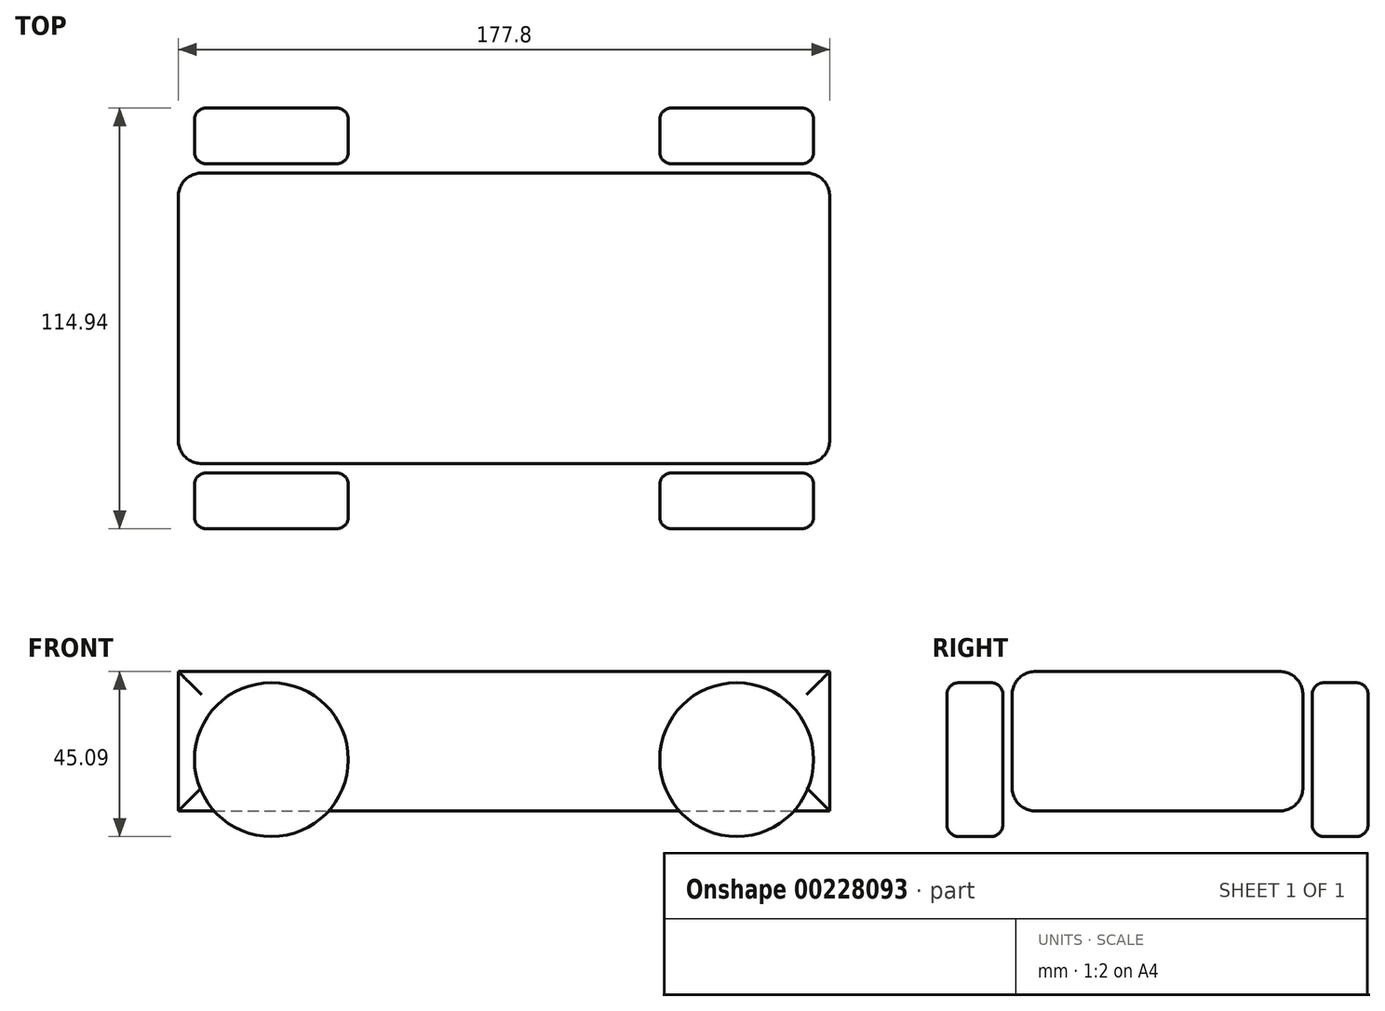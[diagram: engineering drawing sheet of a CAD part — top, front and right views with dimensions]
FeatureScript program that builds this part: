
annotation { "Feature Type Name" : "Feature", "Feature Type Description" : "" }
export const myFeature = defineFeature(function(context is Context, id is Id, definition is map)
    precondition{}
    {
        {
            var Q0;
            Q0=qCreatedBy(makeId("Front.planeOp"),FACE);
            var sketch = newSketch(context, id + "F0", { "sketchPlane" : qUnion([Q0])});
            skLineSegment(sketch, "E0.bottom", {"start": v(-88.9, 19.05) * mm, "end": v(88.9, 19.05) * mm});
            skLineSegment(sketch, "E0.top", {"start": v(-88.9, -19.05) * mm, "end": v(88.9, -19.05) * mm});
            skLineSegment(sketch, "E0.left", {"start": v(-88.9, 19.05) * mm, "end": v(-88.9, -19.05) * mm});
            skLineSegment(sketch, "E0.right", {"start": v(88.9, 19.05) * mm, "end": v(88.9, -19.05) * mm});
            skPoint(sketch, "E0.middle", {"position": v(0, 0) * mm});
            skLineSegment(sketch, "E1", {"start": v(-109.46, -26.03) * mm, "end": v(110.9, -26.04) * mm, "construction": true});
            skCircle(sketch, "E2", {"center": v(63.5, -5.03) * mm, "radius": 21 * mm});
            skSolve(sketch);
        }
        {
            var Q0;
            Q0=qCreatedBy(makeId("Front.planeOp"),FACE);
            var sketch = newSketch(context, id + "F1", { "sketchPlane" : qUnion([Q0])});
            skLineSegment(sketch, "E3.0", {"start": v(-88.9, 19.05) * mm, "end": v(88.9, 19.05) * mm});
            skLineSegment(sketch, "E3.1", {"start": v(-88.9, 19.05) * mm, "end": v(-88.9, -19.05) * mm});
            skLineSegment(sketch, "E3.2", {"start": v(-88.9, -19.05) * mm, "end": v(88.9, -19.05) * mm});
            skLineSegment(sketch, "E3.3", {"start": v(88.9, 19.05) * mm, "end": v(88.9, -19.05) * mm});
            skSolve(sketch);
        }
        {
            var Q0;
            Q0 = qSketchRegion(id + "F1", true);
            extrude(context, id + "F2", {"entities" : qUnion([Q0]), "endBound" : BoundingType.SYMMETRIC, "depth" : 79.38 * mm});
        }
        {
            var Q0;
            Q0=makeQuery(id+"F2.opExtrude","CAP_FACE",FACE,{"disambiguationData":[OSD([sQuery(id+"F1.wireOp",EDGE,"E3.0"),sQuery(id+"F1.wireOp",EDGE,"E3.1"),sQuery(id+"F1.wireOp",EDGE,"E3.2"),sQuery(id+"F1.wireOp",EDGE,"E3.3")])],"isStart":false});
            cPlane(context, id + "F3", {"entities" : qUnion([Q0]), "cplaneType" : CPlaneType.OFFSET, "offset" : 2.54 * mm, "width" : 152.4 * mm, "height" : 152.4 * mm});
        }
        {
            var Q0;
            Q0=qCreatedBy(id+"F3.planeOp",FACE);
            var sketch = newSketch(context, id + "F4", { "sketchPlane" : qUnion([Q0])});
            skCircle(sketch, "E4.0", {"center": v(63.5, -5.03) * mm, "radius": 21 * mm});
            skSolve(sketch);
        }
        {
            var Q0;
            Q0 = qSketchRegion(id + "F4", true);
            extrude(context, id + "F5", {"entities" : qUnion([Q0]), "depth" : 15.24 * mm});
        }
        {
            var Q0;
            Q0=makeQuery(id+"F2.opExtrude","CAP_EDGE",EDGE,{"disambiguationData":[OSD([sQuery(id+"F1.wireOp",EDGE,"E3.0")])],"isStart":false});
            var Q1;
            Q1=makeQuery(id+"F2.opExtrude","CAP_EDGE",EDGE,{"disambiguationData":[OSD([sQuery(id+"F1.wireOp",EDGE,"E3.2")])],"isStart":false});
            var Q2;
            Q2=makeQuery(id+"F2.opExtrude","CAP_EDGE",EDGE,{"disambiguationData":[OSD([sQuery(id+"F1.wireOp",EDGE,"E3.1")])],"isStart":false});
            var Q3;
            Q3=makeQuery(id+"F2.opExtrude","CAP_EDGE",EDGE,{"disambiguationData":[OSD([sQuery(id+"F1.wireOp",EDGE,"E3.3")])],"isStart":false});
            var Q4;
            Q4=makeQuery(id+"F2.opExtrude","CAP_EDGE",EDGE,{"disambiguationData":[OSD([sQuery(id+"F1.wireOp",EDGE,"E3.0")])],"isStart":true});
            var Q5;
            Q5=makeQuery(id+"F2.opExtrude","CAP_EDGE",EDGE,{"disambiguationData":[OSD([sQuery(id+"F1.wireOp",EDGE,"E3.3")])],"isStart":true});
            var Q6;
            Q6=makeQuery(id+"F2.opExtrude","CAP_EDGE",EDGE,{"disambiguationData":[OSD([sQuery(id+"F1.wireOp",EDGE,"E3.2")])],"isStart":true});
            var Q7;
            Q7=makeQuery(id+"F2.opExtrude","CAP_FACE",FACE,{"disambiguationData":[OSD([sQuery(id+"F1.wireOp",EDGE,"E3.0"),sQuery(id+"F1.wireOp",EDGE,"E3.1"),sQuery(id+"F1.wireOp",EDGE,"E3.2"),sQuery(id+"F1.wireOp",EDGE,"E3.3")])],"isStart":true});
            fillet(context, id + "F6", {"entities" : qUnion([Q0, Q1, Q2, Q3, Q4, Q5, Q6, Q7]), "radius" : 6.35 * mm, "tangentPropagation" : true, "allowEdgeOverflow" : false});
        }
        {
            var Q0;
            Q0=makeQuery(id+"F5.opExtrude","CAP_FACE",FACE,{"disambiguationData":[OSD([sQuery(id+"F4.wireOp",EDGE,"E4.0")])],"isStart":false});
            var Q1;
            Q1=makeQuery(id+"F5.opExtrude","CAP_EDGE",EDGE,{"disambiguationData":[OSD([sQuery(id+"F4.wireOp",EDGE,"E4.0")])],"isStart":true});
            fillet(context, id + "F7", {"entities" : qUnion([Q0, Q1]), "radius" : 3.17 * mm, "tangentPropagation" : true, "allowEdgeOverflow" : false});
        }
        {
            var Q0;
            Q0=makeQuery(id+"F5.opExtrude","SWEPT_BODY",BODY,{"disambiguationData":[OSD([sQuery(id+"F4.wireOp",EDGE,"E4.0")])]});
            var Q1;
            Q1=qCreatedBy(makeId("Front.planeOp"),FACE);
            mirror(context, id + "F8", {"entities" : qUnion([Q0]), "mirrorPlane" : qUnion([Q1])});
        }
        {
            var Q0;
            Q0=makeQuery(id+"F5.opExtrude","SWEPT_BODY",BODY,{"disambiguationData":[OSD([sQuery(id+"F4.wireOp",EDGE,"E4.0")])]});
            var Q1;
            Q1=makeQuery(id+"F8.opPattern","COPY",BODY,{"derivedFrom":makeQuery(id+"F5.opExtrude","SWEPT_BODY",BODY,{"disambiguationData":[OSD([sQuery(id+"F4.wireOp",EDGE,"E4.0")])]}),"instanceName":"1"});
            var Q2;
            Q2=qCreatedBy(makeId("Right.planeOp"),FACE);
            mirror(context, id + "F9", {"entities" : qUnion([Q0, Q1]), "mirrorPlane" : qUnion([Q2])});
        }
    });
